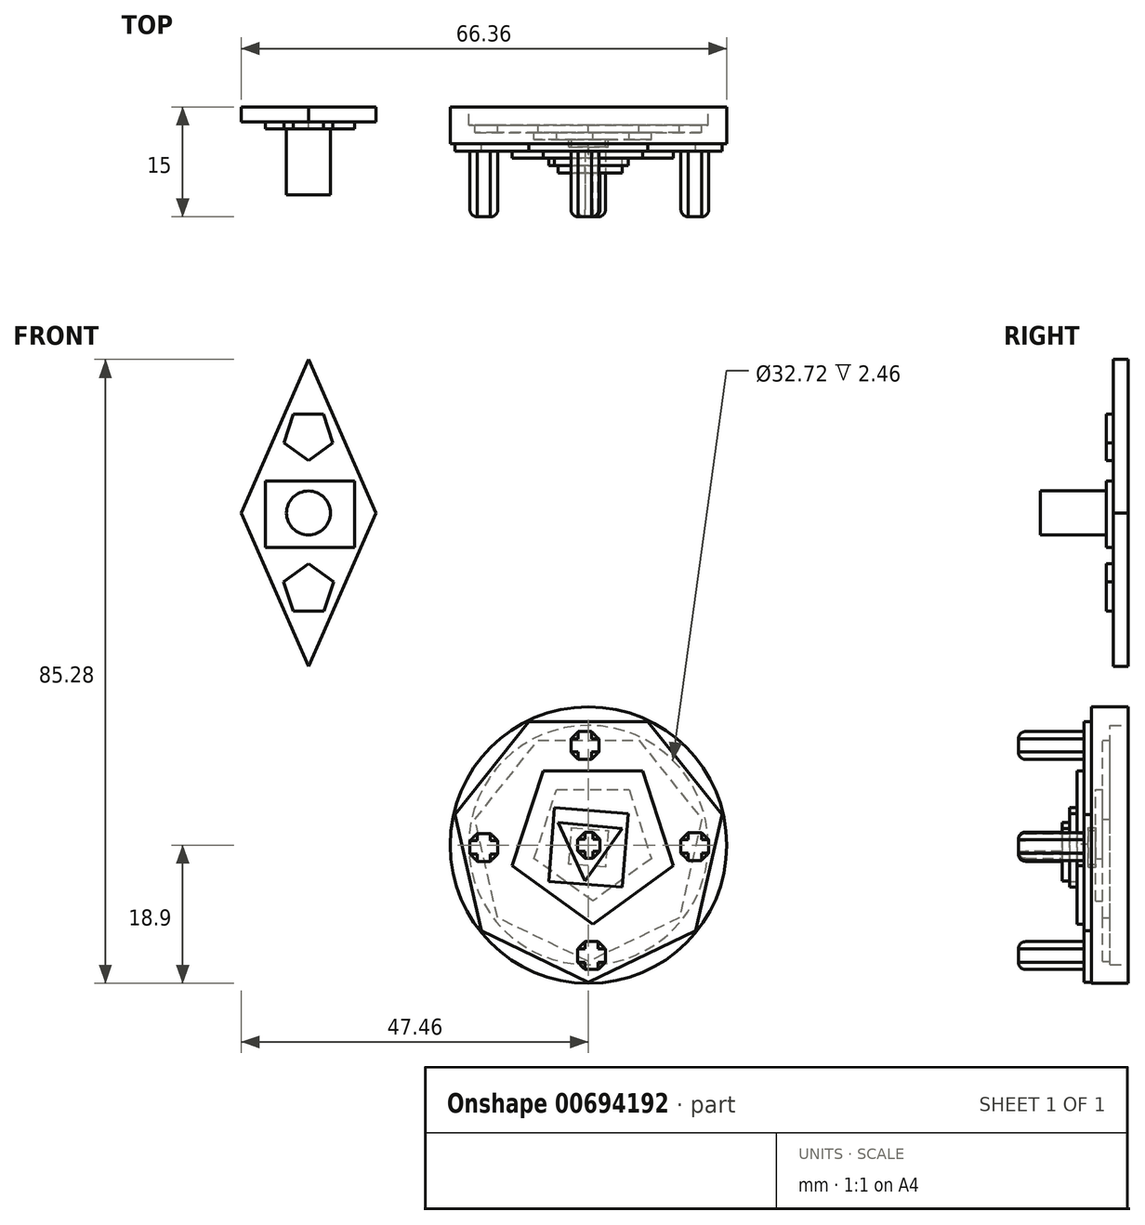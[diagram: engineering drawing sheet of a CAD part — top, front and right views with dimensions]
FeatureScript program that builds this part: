
annotation { "Feature Type Name" : "Feature", "Feature Type Description" : "" }
export const myFeature = defineFeature(function(context is Context, id is Id, definition is map)
    precondition{}
    {
        {
            var Q0;
            Q0=qCreatedBy(makeId("Front.planeOp"),FACE);
            var sketch = newSketch(context, id + "F0", { "sketchPlane" : qUnion([Q0])});
            skCircle(sketch, "E0", {"center": v(0, 0) * mm, "radius": 18.9 * mm});
            skSolve(sketch);
        }
        {
            var Q0;
            Q0 = qSketchRegion(id + "F0", true);
            extrude(context, id + "F1", {"entities" : qUnion([Q0]), "depth" : 5 * mm, "offsetDistance" : 25.4 * mm});
        }
        {
            var Q0;
            Q0=makeQuery(id+"F1.opExtrude","CAP_FACE",FACE,{"disambiguationData":[OSD([sQuery(id+"F0.wireOp",EDGE,"E0")])],"isStart":false});
            var sketch = newSketch(context, id + "F2", { "sketchPlane" : qUnion([Q0])});
            skLineSegment(sketch, "E1.bottom", {"start": v(-1.46, 1.79) * mm, "end": v(1.59, 1.79) * mm});
            skLineSegment(sketch, "E1.top", {"start": v(-1.46, -1.82) * mm, "end": v(1.59, -1.82) * mm});
            skLineSegment(sketch, "E1.left", {"start": v(-1.46, 1.79) * mm, "end": v(-1.46, -1.82) * mm});
            skLineSegment(sketch, "E1.right", {"start": v(1.59, 1.79) * mm, "end": v(1.59, -1.82) * mm});
            skSolve(sketch);
        }
        {
            var Q0;
            Q0=makeQuery(id+"F2.imprint","IMPRINT",FACE,{"disambiguationData":[TD([[makeQuery(id+"F2.imprint","IMPRINT",EDGE,{"derivedFrom":sQuery(id+"F2.wireOp",EDGE,"E1.bottom")}),-1.0]])]});
            extrude(context, id + "F3", {"entities" : qUnion([Q0]), "operationType" : NewBodyOperationType.ADD, "depth" : 10 * mm, "offsetDistance" : 25.4 * mm});
        }
        {
            var Q0;
            Q0=makeQuery(id+"F3.opExtrude","CAP_EDGE",EDGE,{"disambiguationData":[OSD([sQuery(id+"F2.wireOp",EDGE,"E1.left")])],"isStart":false});
            var Q1;
            Q1=makeQuery(id+"F3.opExtrude","CAP_EDGE",EDGE,{"disambiguationData":[OSD([sQuery(id+"F2.wireOp",EDGE,"E1.bottom")])],"isStart":false});
            var Q2;
            Q2=makeQuery(id+"F3.opExtrude","CAP_EDGE",EDGE,{"disambiguationData":[OSD([sQuery(id+"F2.wireOp",EDGE,"E1.right")])],"isStart":false});
            var Q3;
            Q3=makeQuery(id+"F3.opExtrude","CAP_EDGE",EDGE,{"disambiguationData":[OSD([sQuery(id+"F2.wireOp",EDGE,"E1.top")])],"isStart":false});
            fillet(context, id + "F4", {"entities" : qUnion([Q0, Q1, Q2, Q3]), "radius" : 1 * mm, "tangentPropagation" : true, "allowEdgeOverflow" : false});
        }
        {
            var Q0;
            Q0=makeQuery(id+"F3.opExtrude","SWEPT_EDGE",EDGE,{"disambiguationData":[OSD([sQuery(id+"F2.wireOp",EDGE,"E1.bottom"),sQuery(id+"F2.wireOp",EDGE,"E1.right")])]});
            var Q1;
            Q1=makeQuery(id+"F3.opExtrude","SWEPT_EDGE",EDGE,{"disambiguationData":[OSD([sQuery(id+"F2.wireOp",EDGE,"E1.bottom"),sQuery(id+"F2.wireOp",EDGE,"E1.left")])]});
            var Q2;
            Q2=makeQuery(id+"F3.opExtrude","SWEPT_EDGE",EDGE,{"disambiguationData":[OSD([sQuery(id+"F2.wireOp",EDGE,"E1.top"),sQuery(id+"F2.wireOp",EDGE,"E1.right")])]});
            var Q3;
            Q3=makeQuery(id+"F3.opExtrude","SWEPT_EDGE",EDGE,{"disambiguationData":[OSD([sQuery(id+"F2.wireOp",EDGE,"E1.top"),sQuery(id+"F2.wireOp",EDGE,"E1.left")])]});
            chamfer(context, id + "F5", {"entities" : qUnion([Q0, Q1, Q2, Q3]), "width" : 1 * mm, "tangentPropagation" : true});
        }
        {
            var Q0;
            Q0=makeQuery(id+"F1.opExtrude","CAP_FACE",FACE,{"disambiguationData":[OSD([sQuery(id+"F0.wireOp",EDGE,"E0")])],"isStart":false});
            var sketch = newSketch(context, id + "F6", { "sketchPlane" : qUnion([Q0])});
            skLineSegment(sketch, "E2.bottom", {"start": v(-2.4, 15.52) * mm, "end": v(1.41, 15.52) * mm});
            skLineSegment(sketch, "E2.top", {"start": v(-2.4, 11.72) * mm, "end": v(1.41, 11.72) * mm});
            skLineSegment(sketch, "E2.left", {"start": v(-2.4, 15.52) * mm, "end": v(-2.4, 11.72) * mm});
            skLineSegment(sketch, "E2.right", {"start": v(1.41, 15.52) * mm, "end": v(1.41, 11.72) * mm});
            skSolve(sketch);
        }
        {
            var Q0;
            Q0=makeQuery(id+"F6.imprint","IMPRINT",FACE,{"disambiguationData":[TD([[makeQuery(id+"F6.imprint","IMPRINT",EDGE,{"derivedFrom":sQuery(id+"F6.wireOp",EDGE,"E2.bottom")}),1.0]])]});
            var sketch = newSketch(context, id + "F7", { "sketchPlane" : qUnion([Q0])});
            skLineSegment(sketch, "E3.bottom", {"start": v(-16.2, -2.2) * mm, "end": v(-12.4, -2.2) * mm});
            skLineSegment(sketch, "E3.top", {"start": v(-16.2, 1.6) * mm, "end": v(-12.4, 1.6) * mm});
            skLineSegment(sketch, "E3.left", {"start": v(-16.2, -2.2) * mm, "end": v(-16.2, 1.6) * mm});
            skLineSegment(sketch, "E3.right", {"start": v(-12.4, -2.2) * mm, "end": v(-12.4, 1.6) * mm});
            skSolve(sketch);
        }
        {
            var Q0;
            Q0=makeQuery(id+"F6.imprint","IMPRINT",FACE,{"disambiguationData":[TD([[makeQuery(id+"F6.imprint","IMPRINT",EDGE,{"derivedFrom":sQuery(id+"F6.wireOp",EDGE,"E2.bottom")}),1.0]])]});
            var sketch = newSketch(context, id + "F8", { "sketchPlane" : qUnion([Q0])});
            skLineSegment(sketch, "E4.bottom", {"start": v(-1.47, -17) * mm, "end": v(2.33, -17) * mm});
            skLineSegment(sketch, "E4.top", {"start": v(-1.47, -13.2) * mm, "end": v(2.33, -13.2) * mm});
            skLineSegment(sketch, "E4.left", {"start": v(-1.47, -17) * mm, "end": v(-1.47, -13.2) * mm});
            skLineSegment(sketch, "E4.right", {"start": v(2.33, -17) * mm, "end": v(2.33, -13.2) * mm});
            skSolve(sketch);
        }
        {
            var Q0;
            Q0=makeQuery(id+"F6.imprint","IMPRINT",FACE,{"disambiguationData":[TD([[makeQuery(id+"F6.imprint","IMPRINT",EDGE,{"derivedFrom":sQuery(id+"F6.wireOp",EDGE,"E2.bottom")}),1.0]])]});
            var sketch = newSketch(context, id + "F9", { "sketchPlane" : qUnion([Q0])});
            skLineSegment(sketch, "E5.bottom", {"start": v(16.44, -2.09) * mm, "end": v(12.64, -2.09) * mm});
            skLineSegment(sketch, "E5.top", {"start": v(16.44, 1.72) * mm, "end": v(12.64, 1.72) * mm});
            skLineSegment(sketch, "E5.left", {"start": v(16.44, -2.09) * mm, "end": v(16.44, 1.72) * mm});
            skLineSegment(sketch, "E5.right", {"start": v(12.64, -2.09) * mm, "end": v(12.64, 1.72) * mm});
            skSolve(sketch);
        }
        {
            var Q0;
            Q0=makeQuery(id+"F7.imprint","IMPRINT",FACE,{"disambiguationData":[TD([[makeQuery(id+"F7.imprint","IMPRINT",EDGE,{"derivedFrom":sQuery(id+"F7.wireOp",EDGE,"E3.bottom")}),1.0]])]});
            var Q1;
            Q1 = qSketchRegion(id + "F8", true);
            var Q2;
            Q2 = qSketchRegion(id + "F9", true);
            var Q3;
            Q3 = qSketchRegion(id + "F6", true);
            var Q4;
            Q4 = qSketchRegion(id + "F7", true);
            extrude(context, id + "F10", {"entities" : qUnion([Q0, Q1, Q2, Q3, Q4]), "operationType" : NewBodyOperationType.ADD, "depth" : 10 * mm, "offsetDistance" : 25.4 * mm});
        }
        {
            var Q0;
            Q0=makeQuery(id+"F10.opExtrude","CAP_EDGE",EDGE,{"disambiguationData":[OSD([sQuery(id+"F6.wireOp",EDGE,"E2.bottom")])],"isStart":false});
            var Q1;
            Q1=makeQuery(id+"F10.opExtrude","CAP_EDGE",EDGE,{"disambiguationData":[OSD([sQuery(id+"F6.wireOp",EDGE,"E2.right")])],"isStart":false});
            var Q2;
            Q2=makeQuery(id+"F10.opExtrude","CAP_EDGE",EDGE,{"disambiguationData":[OSD([sQuery(id+"F6.wireOp",EDGE,"E2.top")])],"isStart":false});
            var Q3;
            Q3=makeQuery(id+"F10.opExtrude","CAP_EDGE",EDGE,{"disambiguationData":[OSD([sQuery(id+"F6.wireOp",EDGE,"E2.left")])],"isStart":false});
            var Q4;
            Q4=makeQuery(id+"F10.opExtrude","CAP_EDGE",EDGE,{"disambiguationData":[OSD([sQuery(id+"F7.wireOp",EDGE,"E3.top")])],"isStart":false});
            var Q5;
            Q5=makeQuery(id+"F10.opExtrude","CAP_EDGE",EDGE,{"disambiguationData":[OSD([sQuery(id+"F7.wireOp",EDGE,"E3.left")])],"isStart":false});
            var Q6;
            Q6=makeQuery(id+"F10.opExtrude","CAP_EDGE",EDGE,{"disambiguationData":[OSD([sQuery(id+"F7.wireOp",EDGE,"E3.bottom")])],"isStart":false});
            var Q7;
            Q7=makeQuery(id+"F10.opExtrude","CAP_EDGE",EDGE,{"disambiguationData":[OSD([sQuery(id+"F7.wireOp",EDGE,"E3.right")])],"isStart":false});
            var Q8;
            Q8=makeQuery(id+"F10.opExtrude","CAP_EDGE",EDGE,{"disambiguationData":[OSD([sQuery(id+"F9.wireOp",EDGE,"E5.right")])],"isStart":false});
            var Q9;
            Q9=makeQuery(id+"F10.opExtrude","CAP_EDGE",EDGE,{"disambiguationData":[OSD([sQuery(id+"F9.wireOp",EDGE,"E5.top")])],"isStart":false});
            var Q10;
            Q10=makeQuery(id+"F10.opExtrude","CAP_EDGE",EDGE,{"disambiguationData":[OSD([sQuery(id+"F9.wireOp",EDGE,"E5.left")])],"isStart":false});
            var Q11;
            Q11=makeQuery(id+"F10.opExtrude","CAP_EDGE",EDGE,{"disambiguationData":[OSD([sQuery(id+"F9.wireOp",EDGE,"E5.bottom")])],"isStart":false});
            var Q12;
            Q12=makeQuery(id+"F10.opExtrude","CAP_EDGE",EDGE,{"disambiguationData":[OSD([sQuery(id+"F8.wireOp",EDGE,"E4.top")])],"isStart":false});
            var Q13;
            Q13=makeQuery(id+"F10.opExtrude","CAP_EDGE",EDGE,{"disambiguationData":[OSD([sQuery(id+"F8.wireOp",EDGE,"E4.left")])],"isStart":false});
            var Q14;
            Q14=makeQuery(id+"F10.opExtrude","CAP_EDGE",EDGE,{"disambiguationData":[OSD([sQuery(id+"F8.wireOp",EDGE,"E4.right")])],"isStart":false});
            var Q15;
            Q15=makeQuery(id+"F10.opExtrude","CAP_EDGE",EDGE,{"disambiguationData":[OSD([sQuery(id+"F8.wireOp",EDGE,"E4.bottom")])],"isStart":false});
            fillet(context, id + "F11", {"entities" : qUnion([Q0, Q1, Q2, Q3, Q4, Q5, Q6, Q7, Q8, Q9, Q10, Q11, Q12, Q13, Q14, Q15]), "radius" : 1 * mm, "tangentPropagation" : true, "allowEdgeOverflow" : false});
        }
        {
            var Q0;
            Q0=makeQuery(id+"F10.opExtrude","SWEPT_EDGE",EDGE,{"disambiguationData":[OSD([sQuery(id+"F7.wireOp",EDGE,"E3.top"),sQuery(id+"F7.wireOp",EDGE,"E3.left")])]});
            var Q1;
            Q1=makeQuery(id+"F10.opExtrude","SWEPT_EDGE",EDGE,{"disambiguationData":[OSD([sQuery(id+"F7.wireOp",EDGE,"E3.top"),sQuery(id+"F7.wireOp",EDGE,"E3.right")])]});
            var Q2;
            Q2=makeQuery(id+"F10.opExtrude","SWEPT_EDGE",EDGE,{"disambiguationData":[OSD([sQuery(id+"F6.wireOp",EDGE,"E2.bottom"),sQuery(id+"F6.wireOp",EDGE,"E2.left")])]});
            var Q3;
            Q3=makeQuery(id+"F10.opExtrude","SWEPT_EDGE",EDGE,{"disambiguationData":[OSD([sQuery(id+"F6.wireOp",EDGE,"E2.bottom"),sQuery(id+"F6.wireOp",EDGE,"E2.right")])]});
            var Q4;
            Q4=makeQuery(id+"F10.opExtrude","SWEPT_EDGE",EDGE,{"disambiguationData":[OSD([sQuery(id+"F9.wireOp",EDGE,"E5.top"),sQuery(id+"F9.wireOp",EDGE,"E5.right")])]});
            var Q5;
            Q5=makeQuery(id+"F10.opExtrude","SWEPT_EDGE",EDGE,{"disambiguationData":[OSD([sQuery(id+"F9.wireOp",EDGE,"E5.top"),sQuery(id+"F9.wireOp",EDGE,"E5.left")])]});
            var Q6;
            Q6=makeQuery(id+"F10.opExtrude","SWEPT_EDGE",EDGE,{"disambiguationData":[OSD([sQuery(id+"F8.wireOp",EDGE,"E4.top"),sQuery(id+"F8.wireOp",EDGE,"E4.left")])]});
            var Q7;
            Q7=makeQuery(id+"F10.opExtrude","SWEPT_EDGE",EDGE,{"disambiguationData":[OSD([sQuery(id+"F8.wireOp",EDGE,"E4.top"),sQuery(id+"F8.wireOp",EDGE,"E4.right")])]});
            var Q8;
            Q8=makeQuery(id+"F10.opExtrude","SWEPT_EDGE",EDGE,{"disambiguationData":[OSD([sQuery(id+"F7.wireOp",EDGE,"E3.bottom"),sQuery(id+"F7.wireOp",EDGE,"E3.left")])]});
            var Q9;
            Q9=makeQuery(id+"F10.opExtrude","SWEPT_EDGE",EDGE,{"disambiguationData":[OSD([sQuery(id+"F7.wireOp",EDGE,"E3.bottom"),sQuery(id+"F7.wireOp",EDGE,"E3.right")])]});
            var Q10;
            Q10=makeQuery(id+"F10.opExtrude","SWEPT_EDGE",EDGE,{"disambiguationData":[OSD([sQuery(id+"F6.wireOp",EDGE,"E2.top"),sQuery(id+"F6.wireOp",EDGE,"E2.left")])]});
            var Q11;
            Q11=makeQuery(id+"F10.opExtrude","SWEPT_EDGE",EDGE,{"disambiguationData":[OSD([sQuery(id+"F6.wireOp",EDGE,"E2.top"),sQuery(id+"F6.wireOp",EDGE,"E2.right")])]});
            var Q12;
            Q12=makeQuery(id+"F10.opExtrude","SWEPT_EDGE",EDGE,{"disambiguationData":[OSD([sQuery(id+"F9.wireOp",EDGE,"E5.bottom"),sQuery(id+"F9.wireOp",EDGE,"E5.right")])]});
            var Q13;
            Q13=makeQuery(id+"F10.opExtrude","SWEPT_EDGE",EDGE,{"disambiguationData":[OSD([sQuery(id+"F9.wireOp",EDGE,"E5.bottom"),sQuery(id+"F9.wireOp",EDGE,"E5.left")])]});
            var Q14;
            Q14=makeQuery(id+"F10.opExtrude","SWEPT_EDGE",EDGE,{"disambiguationData":[OSD([sQuery(id+"F8.wireOp",EDGE,"E4.bottom"),sQuery(id+"F8.wireOp",EDGE,"E4.right")])]});
            var Q15;
            Q15=makeQuery(id+"F10.opExtrude","SWEPT_EDGE",EDGE,{"disambiguationData":[OSD([sQuery(id+"F8.wireOp",EDGE,"E4.bottom"),sQuery(id+"F8.wireOp",EDGE,"E4.left")])]});
            chamfer(context, id + "F12", {"entities" : qUnion([Q0, Q1, Q2, Q3, Q4, Q5, Q6, Q7, Q8, Q9, Q10, Q11, Q12, Q13, Q14, Q15]), "width" : 1 * mm, "tangentPropagation" : true});
        }
        {
            var Q0;
            Q0=makeQuery(id+"F1.opExtrude","CAP_FACE",FACE,{"disambiguationData":[OSD([sQuery(id+"F0.wireOp",EDGE,"E0")])],"isStart":false});
            var sketch = newSketch(context, id + "F13", { "sketchPlane" : qUnion([Q0])});
            skCircle(sketch, "E6.cCircle", {"center": v(0, 0) * mm, "radius": 16.87 * mm, "construction": true});
            skLineSegment(sketch, "E6.0", {"start": v(-8.12, 16.87) * mm, "end": v(8.12, 16.87) * mm});
            skLineSegment(sketch, "E6.1", {"start": v(8.12, 16.87) * mm, "end": v(18.25, 4.17) * mm});
            skLineSegment(sketch, "E6.2", {"start": v(18.25, 4.17) * mm, "end": v(14.64, -11.67) * mm});
            skLineSegment(sketch, "E6.3", {"start": v(14.64, -11.67) * mm, "end": v(0, -18.72) * mm});
            skLineSegment(sketch, "E6.4", {"start": v(0, -18.72) * mm, "end": v(-14.64, -11.67) * mm});
            skLineSegment(sketch, "E6.5", {"start": v(-14.64, -11.67) * mm, "end": v(-18.25, 4.17) * mm});
            skLineSegment(sketch, "E6.6", {"start": v(-18.25, 4.17) * mm, "end": v(-8.12, 16.87) * mm});
            skPoint(sketch, "E6.0.midPoint", {"position": v(0, 16.87) * mm});
            skSolve(sketch);
        }
        {
            var Q0;
            Q0 = qSketchRegion(id + "F13", true);
            extrude(context, id + "F14", {"entities" : qUnion([Q0]), "operationType" : NewBodyOperationType.ADD, "depth" : 1 * mm, "offsetDistance" : 25.4 * mm});
        }
        {
            var Q0;
            Q0=makeQuery(id+"F14.opExtrude","CAP_FACE",FACE,{"disambiguationData":[OSD([sQuery(id+"F13.wireOp",EDGE,"E6.0"),sQuery(id+"F13.wireOp",EDGE,"E6.1"),sQuery(id+"F13.wireOp",EDGE,"E6.2"),sQuery(id+"F13.wireOp",EDGE,"E6.3"),sQuery(id+"F13.wireOp",EDGE,"E6.4"),sQuery(id+"F13.wireOp",EDGE,"E6.5"),sQuery(id+"F13.wireOp",EDGE,"E6.6")])],"isStart":false});
            var sketch = newSketch(context, id + "F15", { "sketchPlane" : qUnion([Q0])});
            skCircle(sketch, "E7.cCircle", {"center": v(0.59, 0.77) * mm, "radius": 9.36 * mm, "construction": true});
            skLineSegment(sketch, "E7.0", {"start": v(-6.21, 10.13) * mm, "end": v(7.39, 10.13) * mm});
            skLineSegment(sketch, "E7.1", {"start": v(7.39, 10.13) * mm, "end": v(11.6, -2.8) * mm});
            skLineSegment(sketch, "E7.2", {"start": v(11.6, -2.8) * mm, "end": v(0.59, -10.8) * mm});
            skLineSegment(sketch, "E7.3", {"start": v(0.59, -10.8) * mm, "end": v(-10.41, -2.8) * mm});
            skLineSegment(sketch, "E7.4", {"start": v(-10.41, -2.8) * mm, "end": v(-6.21, 10.13) * mm});
            skPoint(sketch, "E7.0.midPoint", {"position": v(0.59, 10.13) * mm});
            skSolve(sketch);
        }
        {
            var Q0;
            Q0=makeQuery(id+"F15.imprint","IMPRINT",FACE,{"disambiguationData":[TD([[makeQuery(id+"F15.imprint","IMPRINT",EDGE,{"derivedFrom":sQuery(id+"F15.wireOp",EDGE,"E7.0")}),-1.0]])]});
            extrude(context, id + "F16", {"entities" : qUnion([Q0]), "operationType" : NewBodyOperationType.ADD, "depth" : 1 * mm, "offsetDistance" : 25.4 * mm});
        }
        {
            var Q0;
            Q0=makeQuery(id+"F16.opExtrude","CAP_FACE",FACE,{"disambiguationData":[OSD([sQuery(id+"F2.wireOp",EDGE,"E1.bottom"),sQuery(id+"F2.wireOp",EDGE,"E1.top"),sQuery(id+"F2.wireOp",EDGE,"E1.left"),sQuery(id+"F2.wireOp",EDGE,"E1.right"),sQuery(id+"F13.wireOp",EDGE,"E6.0"),sQuery(id+"F13.wireOp",EDGE,"E6.1"),sQuery(id+"F13.wireOp",EDGE,"E6.2"),sQuery(id+"F13.wireOp",EDGE,"E6.3"),sQuery(id+"F13.wireOp",EDGE,"E6.4"),sQuery(id+"F13.wireOp",EDGE,"E6.5"),sQuery(id+"F13.wireOp",EDGE,"E6.6"),sQuery(id+"F15.wireOp",EDGE,"E7.0"),sQuery(id+"F15.wireOp",EDGE,"E7.1"),sQuery(id+"F15.wireOp",EDGE,"E7.2"),sQuery(id+"F15.wireOp",EDGE,"E7.3"),sQuery(id+"F15.wireOp",EDGE,"E7.4")])],"isStart":false});
            var sketch = newSketch(context, id + "F17", { "sketchPlane" : qUnion([Q0])});
            skCircle(sketch, "E8.cCircle", {"center": v(0, -0.3) * mm, "radius": 5.05 * mm, "construction": true});
            skLineSegment(sketch, "E8.0", {"start": v(-4.63, 5.13) * mm, "end": v(5.44, 4.32) * mm});
            skLineSegment(sketch, "E8.1", {"start": v(5.44, 4.32) * mm, "end": v(4.63, -5.75) * mm});
            skLineSegment(sketch, "E8.2", {"start": v(4.63, -5.75) * mm, "end": v(-5.44, -4.94) * mm});
            skLineSegment(sketch, "E8.3", {"start": v(-5.44, -4.94) * mm, "end": v(-4.63, 5.13) * mm});
            skPoint(sketch, "E8.0.midPoint", {"position": v(0.4, 4.72) * mm});
            skSolve(sketch);
        }
        {
            var Q0;
            Q0 = qSketchRegion(id + "F17", true);
            extrude(context, id + "F18", {"entities" : qUnion([Q0]), "operationType" : NewBodyOperationType.ADD, "depth" : 1 * mm, "offsetDistance" : 25.4 * mm});
        }
        {
            var Q0;
            Q0=makeQuery(id+"F18.opExtrude","CAP_FACE",FACE,{"disambiguationData":[OSD([sQuery(id+"F17.wireOp",EDGE,"E8.0"),sQuery(id+"F17.wireOp",EDGE,"E8.1"),sQuery(id+"F17.wireOp",EDGE,"E8.2"),sQuery(id+"F17.wireOp",EDGE,"E8.3")])],"isStart":false});
            var sketch = newSketch(context, id + "F19", { "sketchPlane" : qUnion([Q0])});
            skCircle(sketch, "E9.cCircle", {"center": v(0, 0.16) * mm, "radius": 2.55 * mm, "construction": true});
            skLineSegment(sketch, "E9.0", {"start": v(-4.14, 3.12) * mm, "end": v(4.64, 2.27) * mm});
            skLineSegment(sketch, "E9.1", {"start": v(4.64, 2.27) * mm, "end": v(-0.5, -4.91) * mm});
            skLineSegment(sketch, "E9.2", {"start": v(-0.5, -4.91) * mm, "end": v(-4.14, 3.12) * mm});
            skPoint(sketch, "E9.0.midPoint", {"position": v(0.25, 2.7) * mm});
            skSolve(sketch);
        }
        {
            var Q0;
            Q0 = qSketchRegion(id + "F19", true);
            extrude(context, id + "F20", {"entities" : qUnion([Q0]), "operationType" : NewBodyOperationType.ADD, "depth" : 1 * mm, "offsetDistance" : 25.4 * mm});
        }
        {
            var Q0;
            Q0=makeQuery(id+"F1.opExtrude","CAP_FACE",FACE,{"disambiguationData":[OSD([sQuery(id+"F0.wireOp",EDGE,"E0")])],"isStart":true});
            shell(context, id + "F21", {"entities" : qUnion([Q0]), "thickness" : 2.54 * mm});
        }
        {
            var Q0;
            Q0=qCreatedBy(makeId("Front.planeOp"),FACE);
            var sketch = newSketch(context, id + "F22", { "sketchPlane" : qUnion([Q0])});
            skLineSegment(sketch, "E10", {"start": v(-38.26, 66.38) * mm, "end": v(-47.46, 45.4) * mm});
            skLineSegment(sketch, "E11", {"start": v(-47.46, 45.4) * mm, "end": v(-38.26, 24.41) * mm});
            skLineSegment(sketch, "E12", {"start": v(-38.26, 24.41) * mm, "end": v(-29.06, 45.4) * mm});
            skLineSegment(sketch, "E13", {"start": v(-29.06, 45.4) * mm, "end": v(-38.26, 66.38) * mm});
            skSolve(sketch);
        }
        {
            var Q0;
            Q0 = qSketchRegion(id + "F22", true);
            extrude(context, id + "F23", {"entities" : qUnion([Q0]), "depth" : 2 * mm, "offsetDistance" : 25.4 * mm});
        }
        {
            var Q0;
            Q0=makeQuery(id+"F23.opExtrude","CAP_FACE",FACE,{"disambiguationData":[OSD([sQuery(id+"F22.wireOp",EDGE,"E10"),sQuery(id+"F22.wireOp",EDGE,"E11"),sQuery(id+"F22.wireOp",EDGE,"E12"),sQuery(id+"F22.wireOp",EDGE,"E13")])],"isStart":false});
            var sketch = newSketch(context, id + "F24", { "sketchPlane" : qUnion([Q0])});
            skCircle(sketch, "E14", {"center": v(-38.26, 45.4) * mm, "radius": 3 * mm});
            skSolve(sketch);
        }
        {
            var Q0;
            Q0 = qSketchRegion(id + "F24", true);
            extrude(context, id + "F25", {"entities" : qUnion([Q0]), "operationType" : NewBodyOperationType.ADD, "depth" : 10 * mm, "offsetDistance" : 25.4 * mm});
        }
        {
            var Q0;
            Q0=makeQuery(id+"F23.opExtrude","CAP_FACE",FACE,{"disambiguationData":[OSD([sQuery(id+"F22.wireOp",EDGE,"E10"),sQuery(id+"F22.wireOp",EDGE,"E11"),sQuery(id+"F22.wireOp",EDGE,"E12"),sQuery(id+"F22.wireOp",EDGE,"E13")])],"isStart":false});
            var sketch = newSketch(context, id + "F26", { "sketchPlane" : qUnion([Q0])});
            skLineSegment(sketch, "E15.bottom", {"start": v(-44.14, 49.76) * mm, "end": v(-31.95, 49.76) * mm});
            skLineSegment(sketch, "E15.top", {"start": v(-44.14, 40.7) * mm, "end": v(-31.95, 40.7) * mm});
            skLineSegment(sketch, "E15.left", {"start": v(-44.14, 49.76) * mm, "end": v(-44.14, 40.7) * mm});
            skLineSegment(sketch, "E15.right", {"start": v(-31.95, 49.76) * mm, "end": v(-31.95, 40.7) * mm});
            skSolve(sketch);
        }
        {
            var Q0;
            Q0 = qSketchRegion(id + "F26", true);
            extrude(context, id + "F27", {"entities" : qUnion([Q0]), "operationType" : NewBodyOperationType.ADD, "depth" : 1 * mm, "offsetDistance" : 25.4 * mm});
        }
        {
            var Q0;
            Q0=makeQuery(id+"F23.opExtrude","CAP_FACE",FACE,{"disambiguationData":[OSD([sQuery(id+"F22.wireOp",EDGE,"E10"),sQuery(id+"F22.wireOp",EDGE,"E11"),sQuery(id+"F22.wireOp",EDGE,"E12"),sQuery(id+"F22.wireOp",EDGE,"E13")])],"isStart":false});
            var sketch = newSketch(context, id + "F28", { "sketchPlane" : qUnion([Q0])});
            skCircle(sketch, "E16.cCircle", {"center": v(-38.26, 56.08) * mm, "radius": 2.85 * mm, "construction": true});
            skLineSegment(sketch, "E16.0", {"start": v(-40.33, 58.92) * mm, "end": v(-36.2, 58.92) * mm});
            skLineSegment(sketch, "E16.1", {"start": v(-36.2, 58.92) * mm, "end": v(-34.91, 54.99) * mm});
            skLineSegment(sketch, "E16.2", {"start": v(-34.91, 54.99) * mm, "end": v(-38.26, 52.56) * mm});
            skLineSegment(sketch, "E16.3", {"start": v(-38.26, 52.56) * mm, "end": v(-41.6, 54.99) * mm});
            skLineSegment(sketch, "E16.4", {"start": v(-41.6, 54.99) * mm, "end": v(-40.33, 58.92) * mm});
            skPoint(sketch, "E16.0.midPoint", {"position": v(-38.26, 58.92) * mm});
            skSolve(sketch);
        }
        {
            var Q0;
            Q0 = qSketchRegion(id + "F28", true);
            extrude(context, id + "F29", {"entities" : qUnion([Q0]), "operationType" : NewBodyOperationType.ADD, "depth" : 1 * mm, "offsetDistance" : 25.4 * mm});
        }
        {
            var Q0;
            Q0=makeQuery(id+"F23.opExtrude","CAP_FACE",FACE,{"disambiguationData":[OSD([sQuery(id+"F22.wireOp",EDGE,"E10"),sQuery(id+"F22.wireOp",EDGE,"E11"),sQuery(id+"F22.wireOp",EDGE,"E12"),sQuery(id+"F22.wireOp",EDGE,"E13")])],"isStart":false});
            var sketch = newSketch(context, id + "F30", { "sketchPlane" : qUnion([Q0])});
            skCircle(sketch, "E17.cCircle", {"center": v(-38.26, 34.89) * mm, "radius": 2.9 * mm, "construction": true});
            skLineSegment(sketch, "E17.0", {"start": v(-36.15, 31.98) * mm, "end": v(-40.37, 31.98) * mm});
            skLineSegment(sketch, "E17.1", {"start": v(-40.37, 31.98) * mm, "end": v(-41.68, 36) * mm});
            skLineSegment(sketch, "E17.2", {"start": v(-41.68, 36) * mm, "end": v(-38.26, 38.48) * mm});
            skLineSegment(sketch, "E17.3", {"start": v(-38.26, 38.48) * mm, "end": v(-34.84, 36) * mm});
            skLineSegment(sketch, "E17.4", {"start": v(-34.84, 36) * mm, "end": v(-36.15, 31.98) * mm});
            skPoint(sketch, "E17.0.midPoint", {"position": v(-38.26, 31.98) * mm});
            skSolve(sketch);
        }
        {
            var Q0;
            Q0 = qSketchRegion(id + "F30", true);
            extrude(context, id + "F31", {"entities" : qUnion([Q0]), "operationType" : NewBodyOperationType.ADD, "depth" : 1 * mm, "offsetDistance" : 25.4 * mm});
        }
    });
